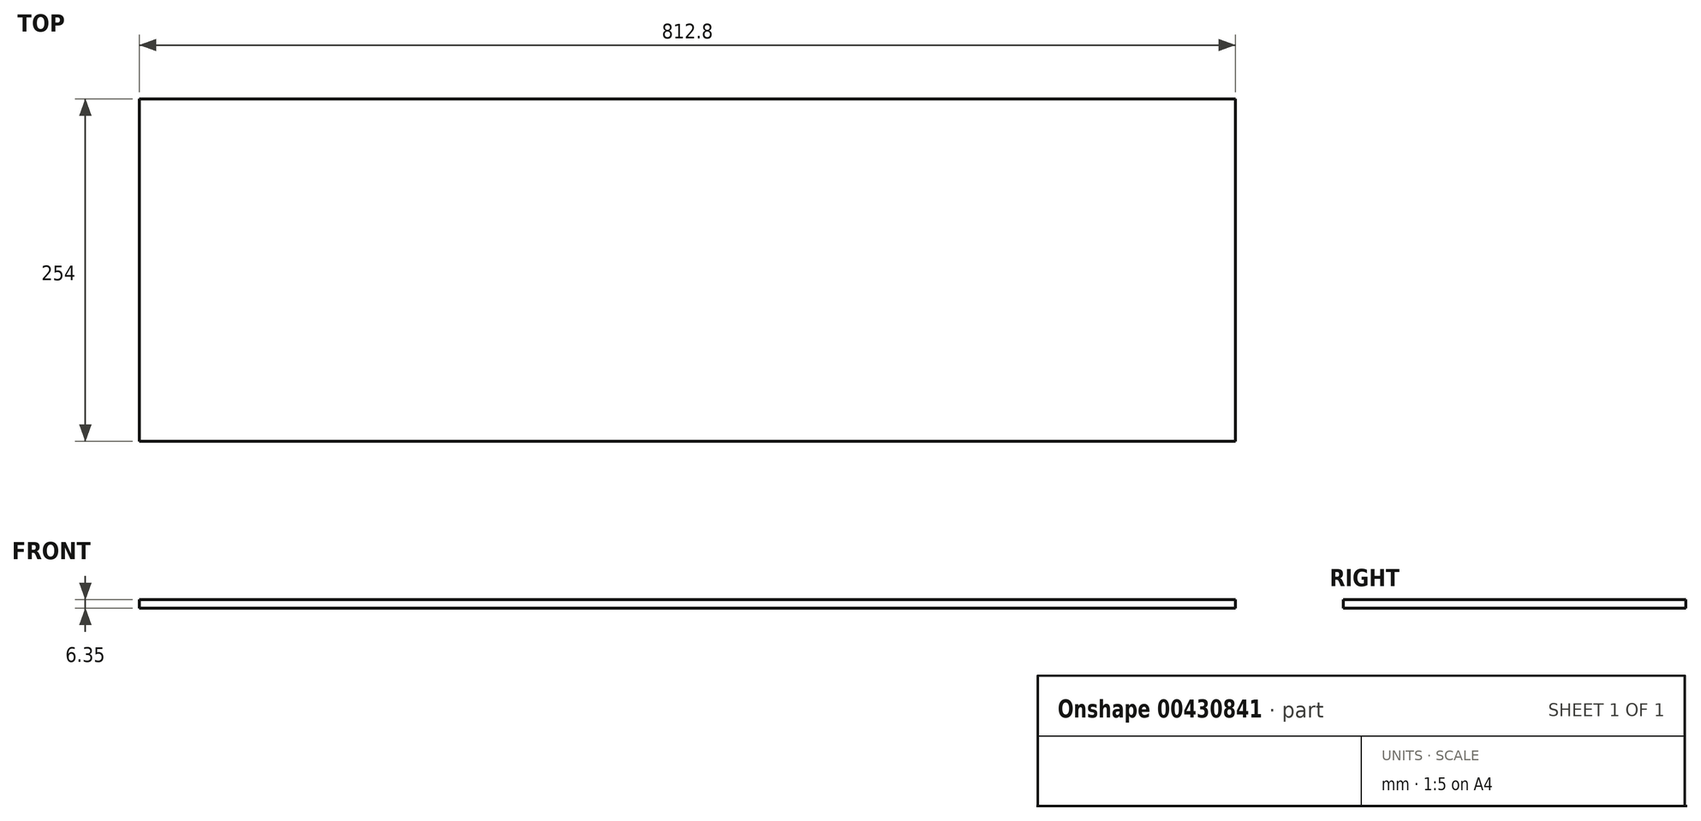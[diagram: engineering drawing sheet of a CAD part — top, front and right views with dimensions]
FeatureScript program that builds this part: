
annotation { "Feature Type Name" : "Feature", "Feature Type Description" : "" }
export const myFeature = defineFeature(function(context is Context, id is Id, definition is map)
    precondition{}
    {
        {
            var Q0;
            Q0=qCreatedBy(makeId("Top.planeOp"),FACE);
            var sketch = newSketch(context, id + "F0", { "sketchPlane" : qUnion([Q0])});
            skLineSegment(sketch, "E0.bottom", {"start": v(406.4, 127) * mm, "end": v(-406.4, 127) * mm});
            skLineSegment(sketch, "E0.top", {"start": v(406.4, -127) * mm, "end": v(-406.4, -127) * mm});
            skLineSegment(sketch, "E0.left", {"start": v(406.4, 127) * mm, "end": v(406.4, -127) * mm});
            skLineSegment(sketch, "E0.right", {"start": v(-406.4, 127) * mm, "end": v(-406.4, -127) * mm});
            skPoint(sketch, "E0.middle", {"position": v(0, 0) * mm});
            skSolve(sketch);
        }
        {
            var Q0;
            Q0=makeQuery(id+"F0.imprint","IMPRINT",FACE,{"disambiguationData":[TD([[makeQuery(id+"F0.imprint","IMPRINT",EDGE,{"derivedFrom":sQuery(id+"F0.wireOp",EDGE,"E0.bottom")}),1.0]])]});
            extrude(context, id + "F1", {"entities" : qUnion([Q0]), "depth" : 6.35 * mm});
        }
    });
